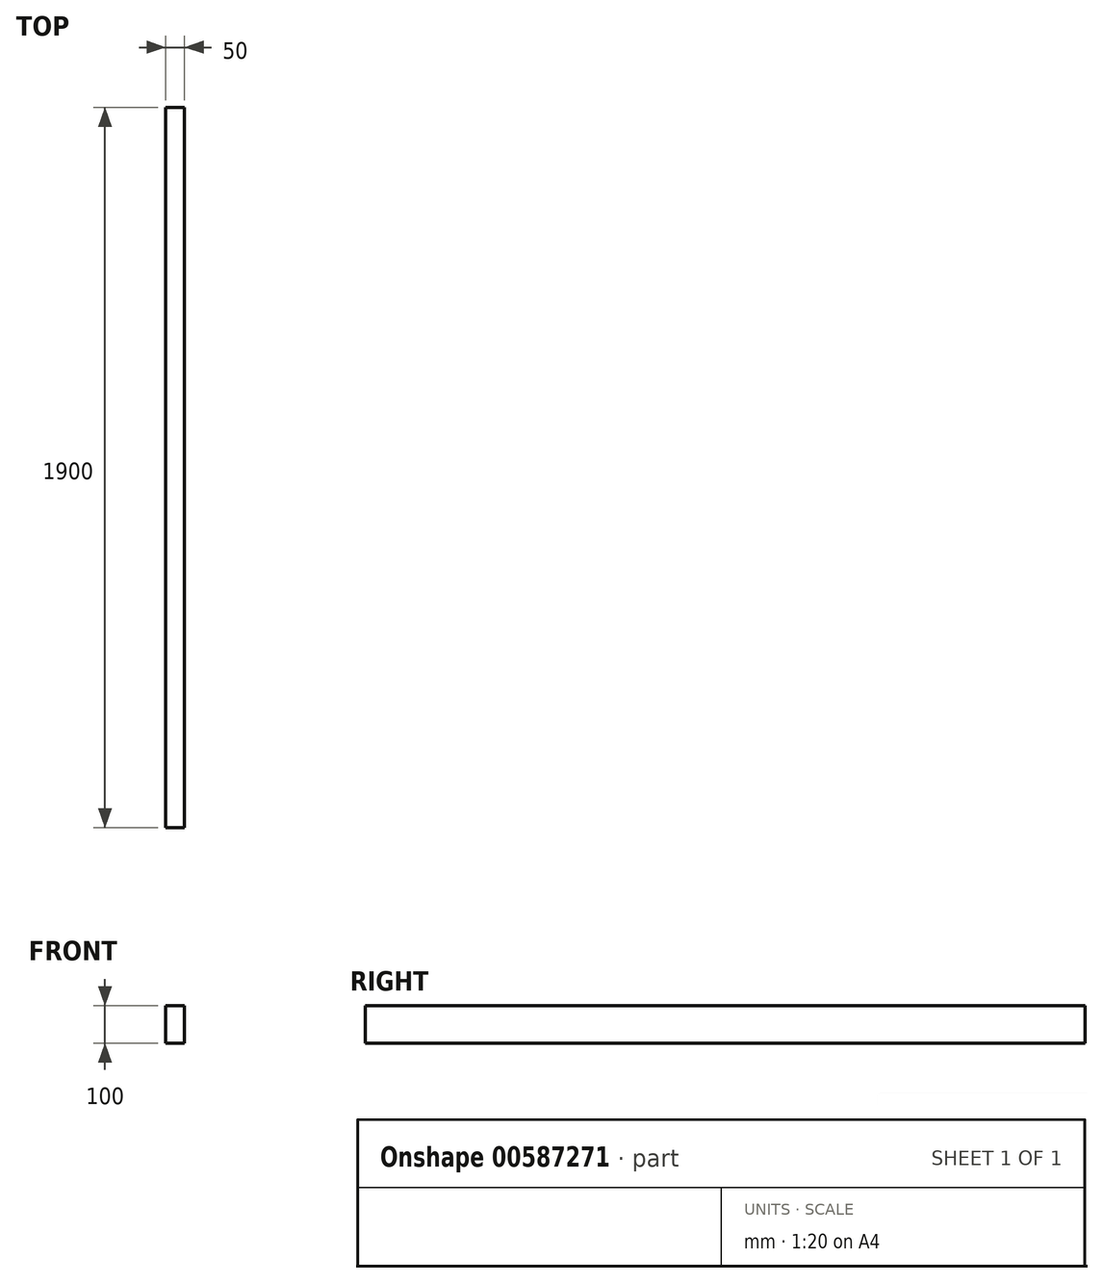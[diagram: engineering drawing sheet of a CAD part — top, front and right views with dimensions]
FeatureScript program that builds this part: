
annotation { "Feature Type Name" : "Feature", "Feature Type Description" : "" }
export const myFeature = defineFeature(function(context is Context, id is Id, definition is map)
    precondition{}
    {
        {
            var Q0;
            Q0=qCreatedBy(makeId("Front.planeOp"),FACE);
            var sketch = newSketch(context, id + "F0", { "sketchPlane" : qUnion([Q0])});
            skLineSegment(sketch, "E0.bottom", {"start": v(25, 50) * mm, "end": v(-25, 50) * mm});
            skLineSegment(sketch, "E0.top", {"start": v(25, -50) * mm, "end": v(-25, -50) * mm});
            skLineSegment(sketch, "E0.left", {"start": v(25, 50) * mm, "end": v(25, -50) * mm});
            skLineSegment(sketch, "E0.right", {"start": v(-25, 50) * mm, "end": v(-25, -50) * mm});
            skPoint(sketch, "E0.middle", {"position": v(0, 0) * mm});
            skSolve(sketch);
        }
        {
            var Q0;
            Q0=makeQuery(id+"F0.imprint","IMPRINT",FACE,{"disambiguationData":[TD([[makeQuery(id+"F0.imprint","IMPRINT",EDGE,{"derivedFrom":sQuery(id+"F0.wireOp",EDGE,"E0.bottom")}),1.0]])]});
            extrude(context, id + "F1", {"entities" : qUnion([Q0]), "endBound" : BoundingType.SYMMETRIC, "depth" : 1900 * mm, "offsetDistance" : 25.4 * mm});
        }
    });
